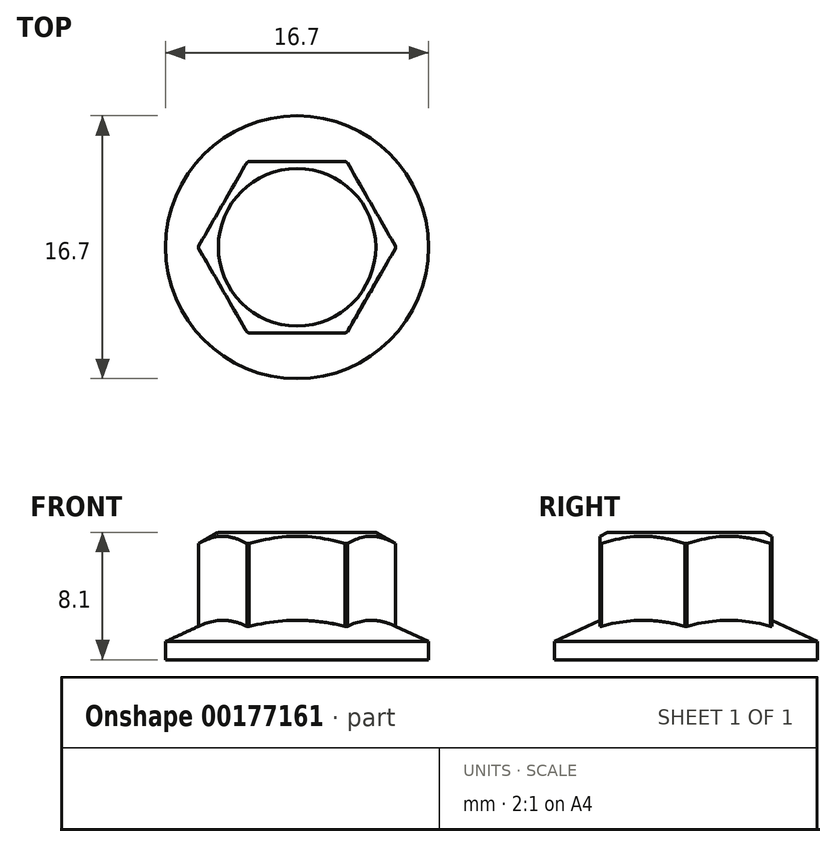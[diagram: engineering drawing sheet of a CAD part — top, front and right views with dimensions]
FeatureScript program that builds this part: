
annotation { "Feature Type Name" : "Feature", "Feature Type Description" : "" }
export const myFeature = defineFeature(function(context is Context, id is Id, definition is map)
    precondition{}
    {
        {
            var Q0;
            Q0=qCreatedBy(makeId("Front.planeOp"),FACE);
            var sketch = newSketch(context, id + "F0", { "sketchPlane" : qUnion([Q0])});
            skLineSegment(sketch, "E0", {"start": v(0, 0) * mm, "end": v(0, 8.1) * mm});
            skLineSegment(sketch, "E1", {"start": v(0, 8.1) * mm, "end": v(5, 8.1) * mm});
            skLineSegment(sketch, "E2", {"start": v(6.25, 7.38) * mm, "end": v(6.25, 2.13) * mm});
            skLineSegment(sketch, "E3", {"start": v(6.25, 2.13) * mm, "end": v(8.35, 1.15) * mm});
            skLineSegment(sketch, "E4", {"start": v(8.35, 1.15) * mm, "end": v(8.35, 0) * mm});
            skLineSegment(sketch, "E5", {"start": v(8.35, 0) * mm, "end": v(0, 0) * mm});
            skLineSegment(sketch, "E6", {"start": v(5, 8.1) * mm, "end": v(6.25, 7.38) * mm});
            skSolve(sketch);
        }
        {
            var Q0;
            Q0=qSketchRegion(id+"F0",true);
            var Q1;
            Q1=sQuery(id+"F0.wireOp",EDGE,"E0");
            revolve(context, id + "F1", {"entities" : qUnion([Q0]), "axis" : qUnion([Q1]), "revolveType" : RevolveType.FULL});
        }
        {
            var Q0;
            Q0=makeQuery(id+"F1.opRevolve","SWEPT_FACE",FACE,{"disambiguationData":[OSD([sQuery(id+"F0.wireOp",EDGE,"E1")])]});
            var sketch = newSketch(context, id + "F2", { "sketchPlane" : qUnion([Q0])});
            skCircle(sketch, "E7.cCircle", {"center": v(0, 0) * mm, "radius": 5.45 * mm, "construction": true});
            skLineSegment(sketch, "E7.0", {"start": v(-3.15, 5.45) * mm, "end": v(3.15, 5.45) * mm});
            skLineSegment(sketch, "E7.1", {"start": v(3.15, 5.45) * mm, "end": v(6.3, 0) * mm});
            skLineSegment(sketch, "E7.2", {"start": v(6.3, 0) * mm, "end": v(3.15, -5.45) * mm});
            skLineSegment(sketch, "E7.3", {"start": v(3.15, -5.45) * mm, "end": v(-3.15, -5.45) * mm});
            skLineSegment(sketch, "E7.4", {"start": v(-3.15, -5.45) * mm, "end": v(-6.3, 0) * mm});
            skLineSegment(sketch, "E7.5", {"start": v(-6.3, 0) * mm, "end": v(-3.15, 5.45) * mm});
            skPoint(sketch, "E7.0.midPoint", {"position": v(0, 5.45) * mm});
            skCircle(sketch, "E8", {"center": v(0, 0) * mm, "radius": 10.58 * mm});
            skSolve(sketch);
        }
        {
            var Q0;
            Q0=qSketchRegion(id+"F2",true);
            var Q1;
            Q1=makeQuery(id+"F1.opRevolve","SWEPT_FACE",FACE,{"disambiguationData":[OSD([sQuery(id+"F0.wireOp",EDGE,"E3")])]});
            extrude(context, id + "F3", {"entities" : qUnion([Q0]), "operationType" : NewBodyOperationType.REMOVE, "endBound" : BoundingType.UP_TO_SURFACE, "oppositeDirection" : true, "endBoundEntityFace" : qUnion([Q1]), "depth" : 25 * mm, "offsetDistance" : 25 * mm});
        }
    });
